# Revit family: Domotics-SerieCivili-GEWISS-27COMBI_SYSTEM-IP55_4P+4P
name_source: partatom
category: Apparecchi elettrici
revit_build: Autodesk Revit 2016 (Build: 20161004_0715(x64)
units: mm (PartAtom-declared; Revit-internal decimal feet)

## family parameters
Condiviso = No
Host = Superficie
Mantenere orientamento annotazione = No
Numero OmniClass = 23.80.30.14.24
Punto di calcolo locali = No
Quota connettore circolare = Usa diametro
Taglio con vuoti quando caricato = Sì
Tipo di parte = Normale
Titolo OmniClass = Junction Boxes

## types (1)
- Domotics-SerieCivili-GEWISS-27COMBI_SYSTEM-IP55_4P+4P
    Catalogo = DOMOTICS
    Catalogo Serie = 27COMBI
    Classe isolamento = II
    Codice EAN = 8011564055407
    Codice Electrocod = 0212
    Colore = Grigio RAL 7035
    Colore portella = Trasparente
    Configurazione = Modulo 4 x 2
    Coppia serraggio viti = 0,8NM
    Descrizione = CONTENITORE 8(4X2) POSTI VERT .STAGNO
    Descrizione: = 8 posti
    Dim. esterne BxHxP (mm) = 132x171x65
    Glow Wire Test = 650°C
    Grado di protezione = IP55
    IDF = 2dc0eff2-1777-4136-a9ab-3e245524659f
    IDT = 3990d046-d57d-4ccd-aa40-94a36558d188
    Immagine tipo = gw27051.jpg
    Modello = GW27051
    N. fori Ã˜ 23 sfondabili: = Laterali 10 / Sul fondo 2
    N. moduli SYSTEM = 8 posti
    Norma di riferimento: = EN 60670-1
    Predisposizione scomparti = 2
    Produttore = GEWISS S.p.A.
    Prospetto di default = 1219 mm
    Resistenza agli urti = IK07
    SEO = Contenitore
    Scheda Tecnica = https://www.gewiss.com
    Temperatura di installazione = -25 +60 °C
    Termopressione con biglia = 70 °C
    Tipo portella = Con membrana
    Tipo sfondabili = Asportabili con utensile
    URL = https://www.gewiss.com
    Versione file RFA = 19.4
    Viti coperchio = Acciaio inox
